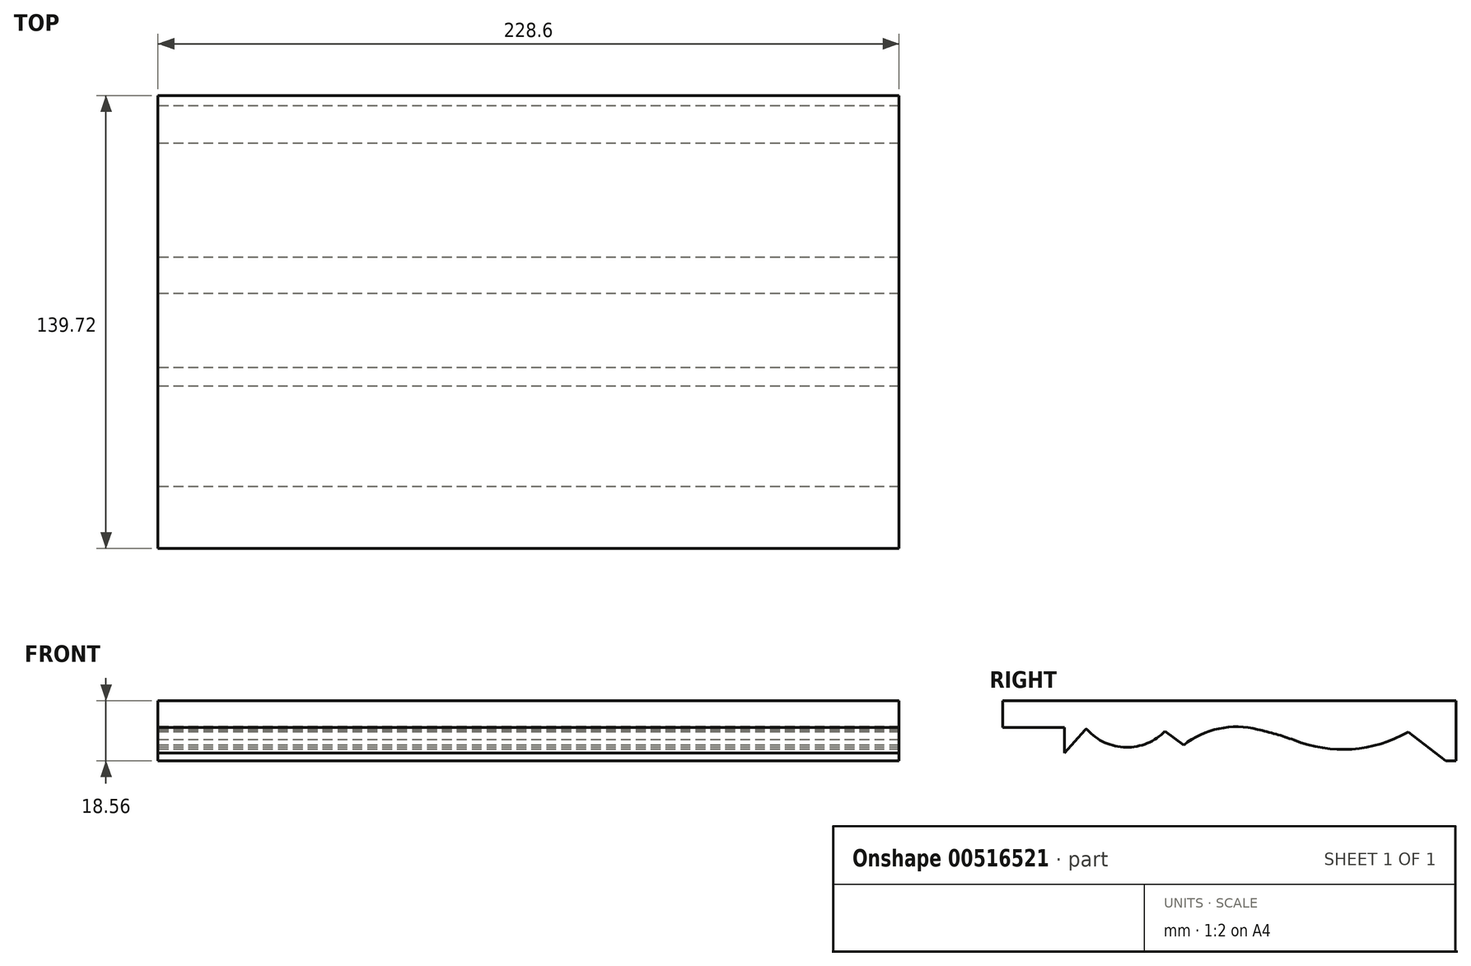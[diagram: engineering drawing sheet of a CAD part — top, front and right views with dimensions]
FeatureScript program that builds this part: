
annotation { "Feature Type Name" : "Feature", "Feature Type Description" : "" }
export const myFeature = defineFeature(function(context is Context, id is Id, definition is map)
    precondition{}
    {
        {
            var Q0;
            Q0=qCreatedBy(makeId("Right.planeOp"),FACE);
            var sketch = newSketch(context, id + "F0", { "sketchPlane" : qUnion([Q0])});
            skLineSegment(sketch, "E0", {"start": v(50.6, 7.46) * mm, "end": v(62.12, -1.48) * mm});
            skLineSegment(sketch, "E1", {"start": v(-55.37, 0.9) * mm, "end": v(-49.1, 8.1) * mm});
            skArc(sketch, "E2", {"start": v(-48.34, 8.1) * mm, "mid": v(-36.45, 2.71) * mm, "end": v(-24.39, 7.71) * mm});
            skLineSegment(sketch, "E3", {"start": v(-24.39, 7.71) * mm, "end": v(-18.62, 3.42) * mm});
            skArc(sketch, "E4", {"start": v(4.18, 8.24) * mm, "mid": v(-7.78, 8.48) * mm, "end": v(-18.62, 3.42) * mm});
            skArc(sketch, "E5", {"start": v(15.34, 4.97) * mm, "mid": v(9.8, 6.76) * mm, "end": v(4.18, 8.24) * mm});
            skArc(sketch, "E6", {"start": v(15.34, 4.97) * mm, "mid": v(33.25, 2.15) * mm, "end": v(50.6, 7.46) * mm});
            skLineSegment(sketch, "E7", {"start": v(-55.37, 0.9) * mm, "end": v(-55.37, 8.83) * mm});
            skLineSegment(sketch, "E8", {"start": v(-55.37, 8.83) * mm, "end": v(-74.42, 8.83) * mm});
            skLineSegment(sketch, "E9", {"start": v(-74.42, 17.08) * mm, "end": v(-74.42, 8.83) * mm});
            skLineSegment(sketch, "E10", {"start": v(62.12, -1.48) * mm, "end": v(65.3, -1.48) * mm});
            skArc(sketch, "E11", {"start": v(-48.34, 8.1) * mm, "mid": v(-48.72, 8.27) * mm, "end": v(-49.1, 8.1) * mm});
            skLineSegment(sketch, "E12", {"start": v(-74.42, 17.08) * mm, "end": v(65.3, 17.08) * mm});
            skLineSegment(sketch, "E13", {"start": v(65.3, 17.08) * mm, "end": v(65.3, -1.48) * mm});
            skSolve(sketch);
        }
        {
            var Q0;
            Q0 = qSketchRegion(id + "F0", true);
            extrude(context, id + "F1", {"entities" : qUnion([Q0]), "depth" : 114.3 * mm, "offsetDistance" : 25.4 * mm});
        }
        {
            var Q0;
            Q0=makeQuery(id+"F1.opExtrude","CAP_FACE",FACE,{"disambiguationData":[OSD([sQuery(id+"F0.wireOp",EDGE,"E0"),sQuery(id+"F0.wireOp",EDGE,"E1"),sQuery(id+"F0.wireOp",EDGE,"E2"),sQuery(id+"F0.wireOp",EDGE,"E3"),sQuery(id+"F0.wireOp",EDGE,"E4"),sQuery(id+"F0.wireOp",EDGE,"E5"),sQuery(id+"F0.wireOp",EDGE,"E6"),sQuery(id+"F0.wireOp",EDGE,"E7"),sQuery(id+"F0.wireOp",EDGE,"E8"),sQuery(id+"F0.wireOp",EDGE,"E9"),sQuery(id+"F0.wireOp",EDGE,"E10"),sQuery(id+"F0.wireOp",EDGE,"E11"),sQuery(id+"F0.wireOp",EDGE,"E12"),sQuery(id+"F0.wireOp",EDGE,"E13")])],"isStart":true});
            extrude(context, id + "F2", {"entities" : qUnion([Q0]), "operationType" : NewBodyOperationType.ADD, "depth" : 114.3 * mm, "offsetDistance" : 25.4 * mm});
        }
    });
